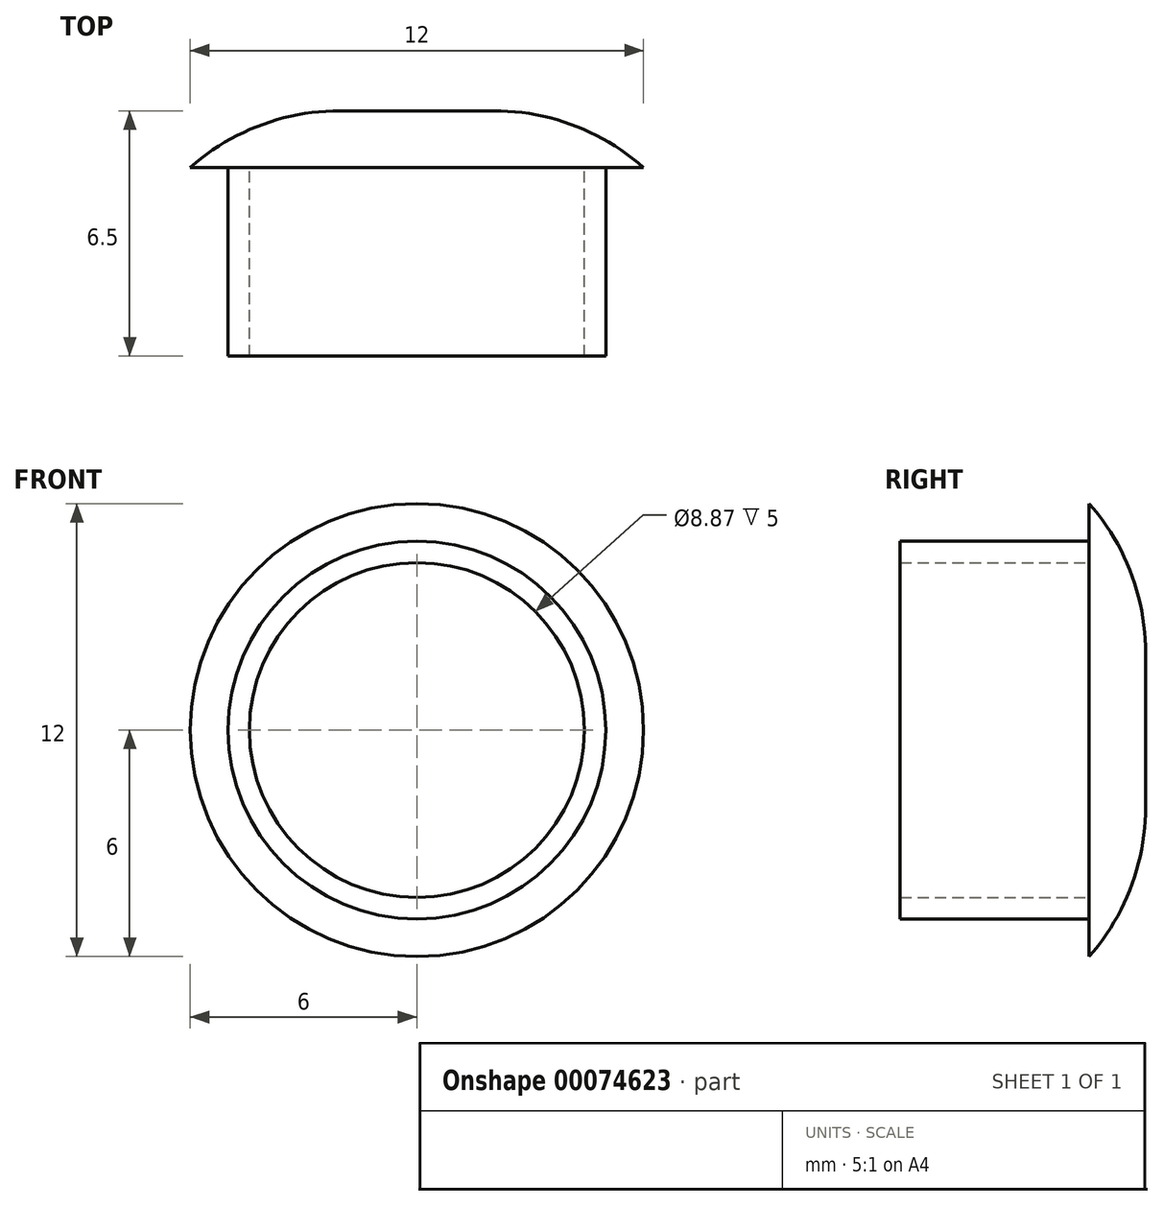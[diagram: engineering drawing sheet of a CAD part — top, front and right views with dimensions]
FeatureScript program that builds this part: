
annotation { "Feature Type Name" : "Feature", "Feature Type Description" : "" }
export const myFeature = defineFeature(function(context is Context, id is Id, definition is map)
    precondition{}
    {
        {
            var Q0;
            Q0=qCreatedBy(makeId("Front.planeOp"),FACE);
            var sketch = newSketch(context, id + "F0", { "sketchPlane" : qUnion([Q0])});
            skCircle(sketch, "E0", {"center": v(0, 0) * mm, "radius": 5 * mm});
            skCircle(sketch, "E1", {"center": v(0, 0) * mm, "radius": 4.43 * mm});
            skSolve(sketch);
        }
        {
            var Q0;
            Q0=makeQuery(id+"F0.imprint","IMPRINT",FACE,{"disambiguationData":[TD([[makeQuery(id+"F0.imprint","IMPRINT",EDGE,{"derivedFrom":sQuery(id+"F0.wireOp",EDGE,"E0")}),1.0]])]});
            extrude(context, id + "F1", {"entities" : qUnion([Q0]), "depth" : 5 * mm});
        }
        {
            var Q0;
            Q0=qCreatedBy(makeId("Front.planeOp"),FACE);
            var sketch = newSketch(context, id + "F2", { "sketchPlane" : qUnion([Q0])});
            skCircle(sketch, "E2", {"center": v(0, 0) * mm, "radius": 6 * mm});
            skSolve(sketch);
        }
        {
            var Q0;
            Q0=makeQuery(id+"F2.imprint","IMPRINT",FACE,{"disambiguationData":[TD([[makeQuery(id+"F2.imprint","IMPRINT",EDGE,{"derivedFrom":sQuery(id+"F2.wireOp",EDGE,"E2")}),1.0]])]});
            extrude(context, id + "F3", {"entities" : qUnion([Q0]), "operationType" : NewBodyOperationType.ADD, "oppositeDirection" : true, "depth" : 1.5 * mm});
        }
        {
            var Q0;
            Q0=makeQuery(id+"F3.opExtrude","CAP_EDGE",EDGE,{"disambiguationData":[OSD([sQuery(id+"F2.wireOp",EDGE,"E2")])],"isStart":false});
            fillet(context, id + "F4", {"entities" : qUnion([Q0]), "radius" : 6 * mm, "tangentPropagation" : true, "allowEdgeOverflow" : false});
        }
    });
